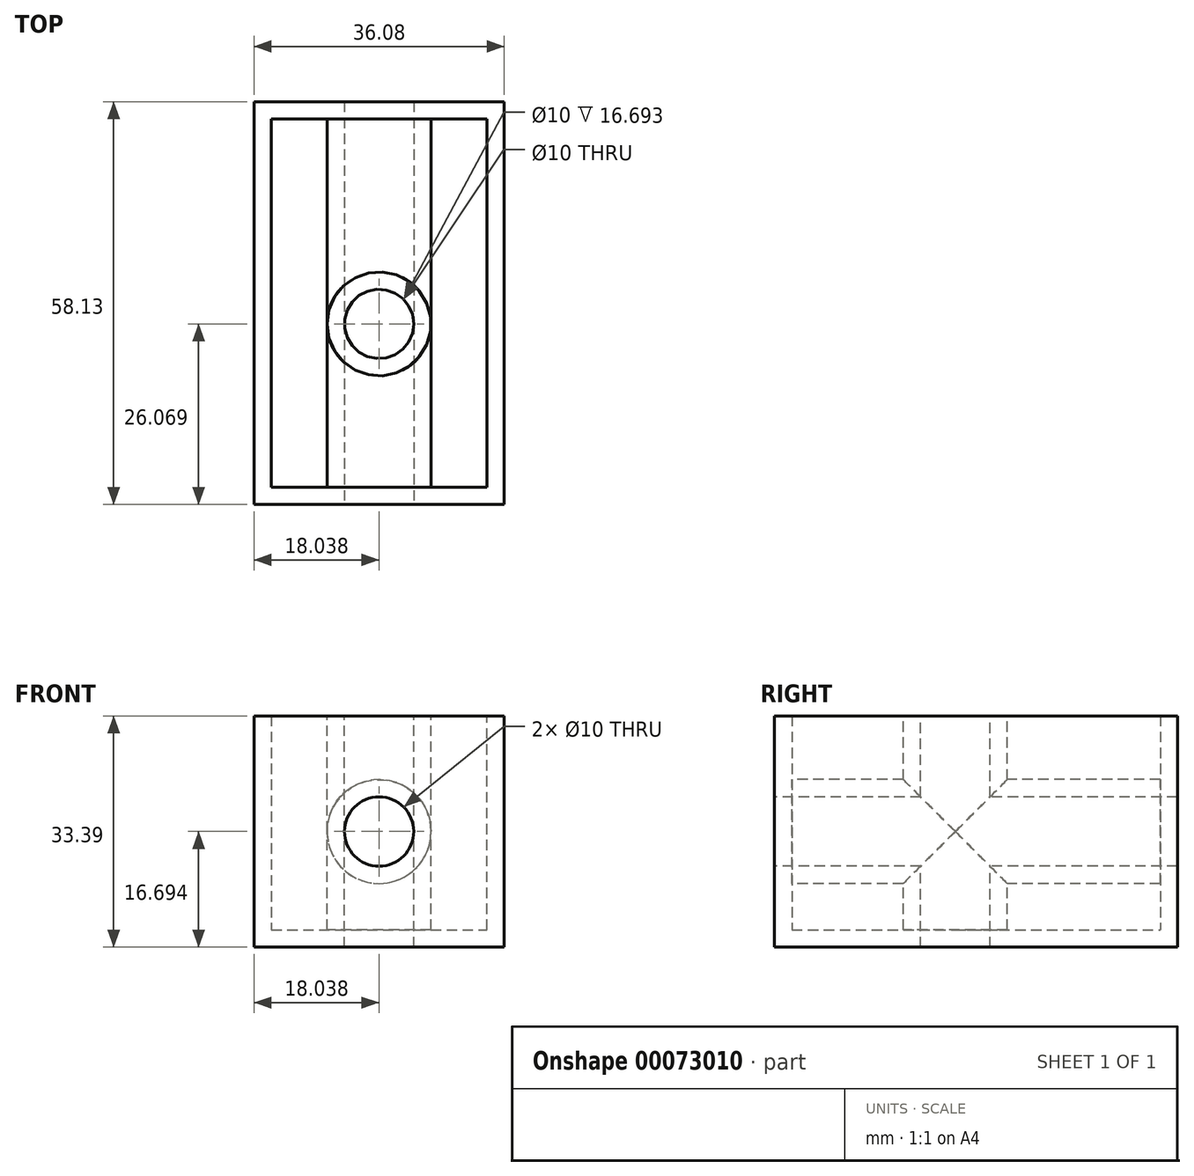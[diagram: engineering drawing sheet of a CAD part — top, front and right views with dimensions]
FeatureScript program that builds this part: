
annotation { "Feature Type Name" : "Feature", "Feature Type Description" : "" }
export const myFeature = defineFeature(function(context is Context, id is Id, definition is map)
    precondition{}
    {
        {
            var Q0;
            Q0=qCreatedBy(makeId("Front.planeOp"),FACE);
            var sketch = newSketch(context, id + "F0", { "sketchPlane" : qUnion([Q0])});
            skLineSegment(sketch, "E0", {"start": v(0, 0) * mm, "end": v(36.08, 0) * mm});
            skLineSegment(sketch, "E1", {"start": v(36.08, 0) * mm, "end": v(36.08, 33.39) * mm});
            skLineSegment(sketch, "E2", {"start": v(36.08, 33.39) * mm, "end": v(0, 33.39) * mm});
            skLineSegment(sketch, "E3", {"start": v(0, 33.39) * mm, "end": v(0, 0) * mm});
            skSolve(sketch);
        }
        {
            var Q0;
            Q0=makeQuery(id+"F0.imprint","IMPRINT",FACE,{"disambiguationData":[TD([[makeQuery(id+"F0.imprint","IMPRINT",EDGE,{"derivedFrom":sQuery(id+"F0.wireOp",EDGE,"E0")}),1.0]])]});
            extrude(context, id + "F1", {"entities" : qUnion([Q0]), "depth" : 58.13 * mm});
        }
        {
            var Q0;
            Q0=makeQuery(id+"F1.opExtrude","SWEPT_FACE",FACE,{"disambiguationData":[OSD([sQuery(id+"F0.wireOp",EDGE,"E2")])]});
            var sketch = newSketch(context, id + "F2", { "sketchPlane" : qUnion([Q0])});
            skCircle(sketch, "E4", {"center": v(18.04, -32.06) * mm, "radius": 6.05 * mm});
            skPoint(sketch, "E4.centerSnap0", {"position": v(18.04, 0) * mm});
            skSolve(sketch);
        }
        {
            var Q0;
            Q0=sQuery(id+"F2.wireOp",VERTEX,"E4.center");
            var Q1;
            Q1=makeQuery(id+"F1.opExtrude","SWEPT_BODY",BODY,{"disambiguationData":[OSD([sQuery(id+"F0.wireOp",EDGE,"E0"),sQuery(id+"F0.wireOp",EDGE,"E1"),sQuery(id+"F0.wireOp",EDGE,"E2"),sQuery(id+"F0.wireOp",EDGE,"E3")])]});
            hole(context, id + "F3", {"style" : HoleStyle.SIMPLE, "holeDiameter" : 10 * mm, "endStyle" : HoleEndStyle.THROUGH, "locations" : qUnion([Q0]), "scope" : qUnion([Q1])});
        }
        {
            var Q0;
            Q0=makeQuery(id+"F1.opExtrude","CAP_FACE",FACE,{"disambiguationData":[OSD([sQuery(id+"F0.wireOp",EDGE,"E0"),sQuery(id+"F0.wireOp",EDGE,"E1"),sQuery(id+"F0.wireOp",EDGE,"E2"),sQuery(id+"F0.wireOp",EDGE,"E3")])],"isStart":false});
            var sketch = newSketch(context, id + "F4", { "sketchPlane" : qUnion([Q0])});
            skPoint(sketch, "E5", {"position": v(18.04, 16.7) * mm});
            skPoint(sketch, "E5.positionSnap0", {"position": v(18.04, 33.39) * mm});
            skPoint(sketch, "E5.positionSnap1", {"position": v(36.08, 16.7) * mm});
            skCircle(sketch, "E6", {"center": v(18.04, 16.7) * mm, "radius": 7.35 * mm});
            skSolve(sketch);
        }
        {
            var Q0;
            Q0=sQuery(id+"F4.wireOp",VERTEX,"E5");
            var Q1;
            Q1=makeQuery(id+"F1.opExtrude","SWEPT_BODY",BODY,{"disambiguationData":[OSD([sQuery(id+"F0.wireOp",EDGE,"E0"),sQuery(id+"F0.wireOp",EDGE,"E1"),sQuery(id+"F0.wireOp",EDGE,"E2"),sQuery(id+"F0.wireOp",EDGE,"E3")])]});
            hole(context, id + "F5", {"style" : HoleStyle.SIMPLE, "holeDiameter" : 10 * mm, "endStyle" : HoleEndStyle.THROUGH, "locations" : qUnion([Q0]), "scope" : qUnion([Q1])});
        }
        {
            var Q0;
            Q0=makeQuery(id+"F1.opExtrude","SWEPT_FACE",FACE,{"disambiguationData":[OSD([sQuery(id+"F0.wireOp",EDGE,"E2")])]});
            shell(context, id + "F6", {"entities" : qUnion([Q0]), "thickness" : 2.5 * mm});
        }
    });
